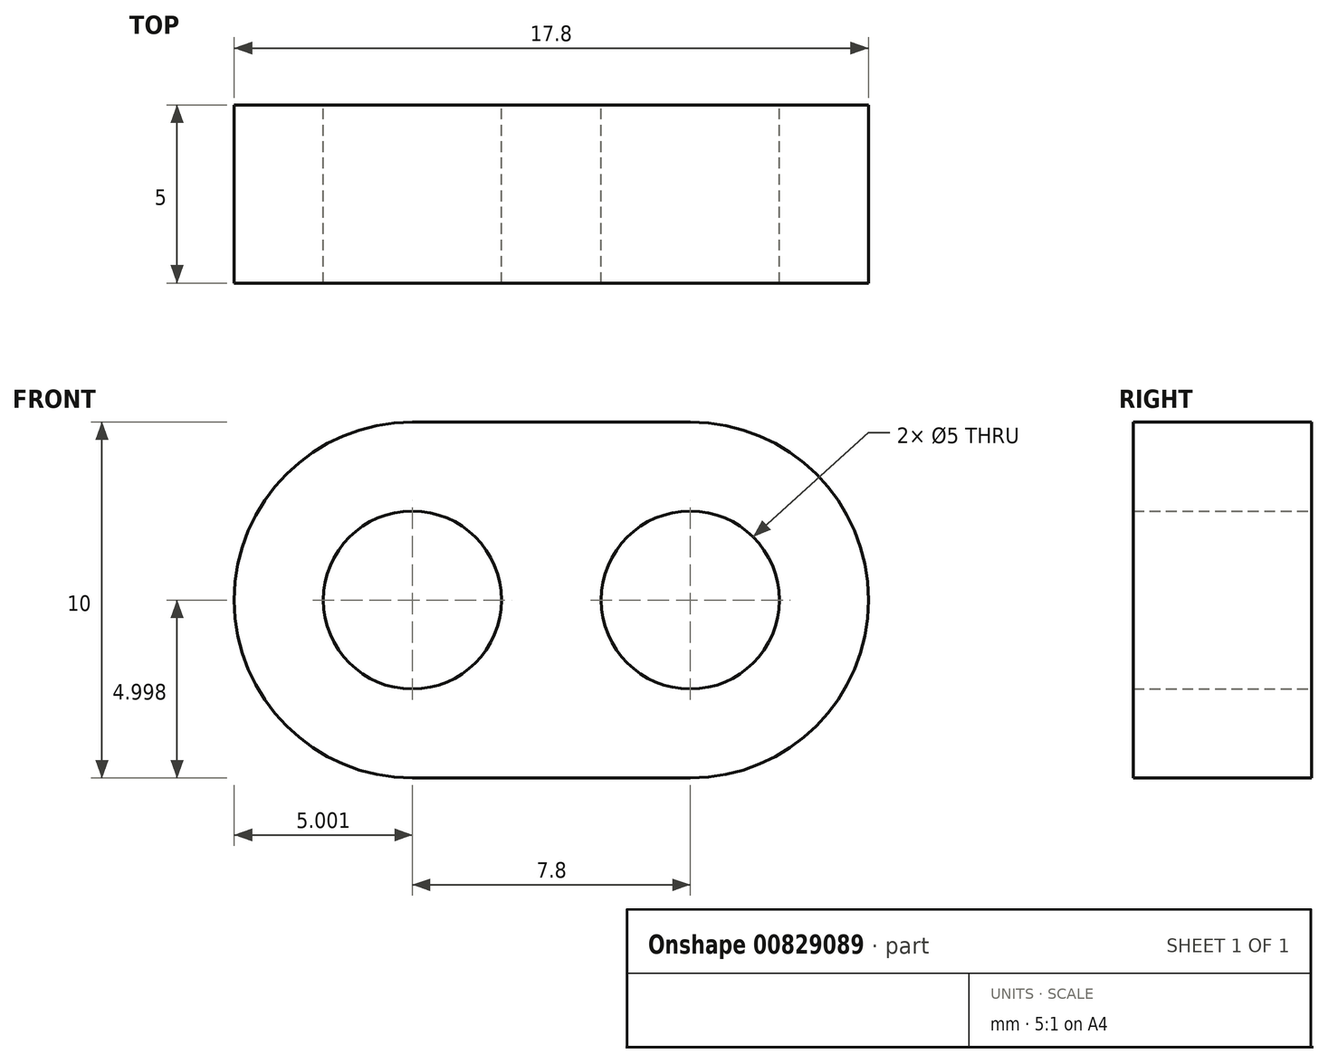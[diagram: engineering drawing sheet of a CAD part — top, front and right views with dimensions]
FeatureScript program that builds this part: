
annotation { "Feature Type Name" : "Feature", "Feature Type Description" : "" }
export const myFeature = defineFeature(function(context is Context, id is Id, definition is map)
    precondition{}
    {
        {
            var Q0;
            Q0=qCreatedBy(makeId("Front.planeOp"),FACE);
            var sketch = newSketch(context, id + "F0", { "sketchPlane" : qUnion([Q0])});
            skArc(sketch, "E0", {"start": v(-15.63, 13.86) * mm, "mid": v(-20.63, 8.86) * mm, "end": v(-15.63, 3.86) * mm});
            skArc(sketch, "E1", {"start": v(-7.83, 3.86) * mm, "mid": v(-2.83, 8.86) * mm, "end": v(-7.83, 13.86) * mm});
            skLineSegment(sketch, "E2", {"start": v(-15.63, 13.86) * mm, "end": v(-7.83, 13.86) * mm});
            skLineSegment(sketch, "E3", {"start": v(-15.63, 3.86) * mm, "end": v(-7.83, 3.86) * mm});
            skCircle(sketch, "E4", {"center": v(-15.63, 8.86) * mm, "radius": 2.5 * mm});
            skCircle(sketch, "E5", {"center": v(-7.83, 8.86) * mm, "radius": 2.5 * mm});
            skSolve(sketch);
        }
        {
            var Q0;
            Q0 = qSketchRegion(id + "F0", true);
            extrude(context, id + "F1", {"entities" : qUnion([Q0]), "depth" : 5 * mm, "offsetDistance" : 25 * mm});
        }
    });
